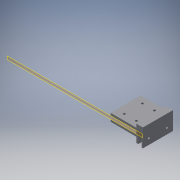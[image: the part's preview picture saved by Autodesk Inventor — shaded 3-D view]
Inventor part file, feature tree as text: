
AUTODESK INVENTOR PART (.ipt)
format: ipt  version: 2016 (Build 200138000, 138)  size: 224,256 bytes
history: native  units: in
note: dims shown in document units (in); Inventor stores cm internally (conversion verified against a paired STEP export)
features: reference x12, sketch x8, extrude x7, projected_geometry x4, plane x3, fillet x1, chamfer x1
ambient origin geometry x8: Origin, YZ Plane, XZ Plane, XY Plane, X Axis, Y Axis, Z Axis, Center Point
bodies: Solid1 (feature_tree)
feature tree (36):
  plane  "Work Plane1"
  sketch  "Sketch1"  dims[d0=0.3in d1=0.15in]
  plane  "Work Plane2"
  extrude  "Extrusion1"  Depth=0.15in
  extrude  "Extrusion2"  Depth=0.2in
  extrude  "Extrusion3"  Depth=0.25in
  sketch  "Sketch4"  dims[d6=90.0deg d7=0.2in]
  extrude  "Extrusion4"  Depth=0.2in
  extrude  "Extrusion5"  Depth=0.05in
  fillet  "Fillet1"  Radius=1.0in
  extrude  "Extrusion6"  Depth=1.5in
  plane  "Work Plane3"
  extrude  "Extrusion7"  Depth=2.0in TaperAngle=0.0deg
  chamfer  "Chamfer1"  Distance=2.0in
  reference  "Reference1"
  reference  "Reference2"
  reference  "Reference3"
  reference  "Reference4"
  reference  "Reference5"
  reference  "Reference6"
  sketch  "Sketch2"  dims[d2=0.2in d3=2.15in]
  reference  "Reference7"
  reference  "Reference8"
  reference  "Reference9"
  reference  "Reference10"
  sketch  "Sketch3"  dims[d4=90.0deg d5=0.25in]
  reference  "Reference11"
  reference  "Reference12"
  sketch  "Sketch5"  dims[d8=90.0deg d9=0.05in d10=1.0in]
  projected_geometry  "Projected Loop1"
  sketch  "Sketch6"  dims[d11=0.1in d12=1.5in]
  projected_geometry  "Projected Loop2"
  sketch  "Sketch7"  dims[d13=0.1in d14=1.0in d15=0.0in d16=2.0in d17=0.0in]
  projected_geometry  "Projected Loop3"
  sketch  "Sketch8"  dims[d18=0.75in d19=0.0in d20=1.0in d21=0.0in d22=1.4375in d23=0.0in d24=0.5in d25=0.2in d26=0.0in d27=1.5in d28=0.2in d29=0.0in d30=0.6875in d31=0.125in d32=45.0deg]
  projected_geometry  "Projected Loop4"
